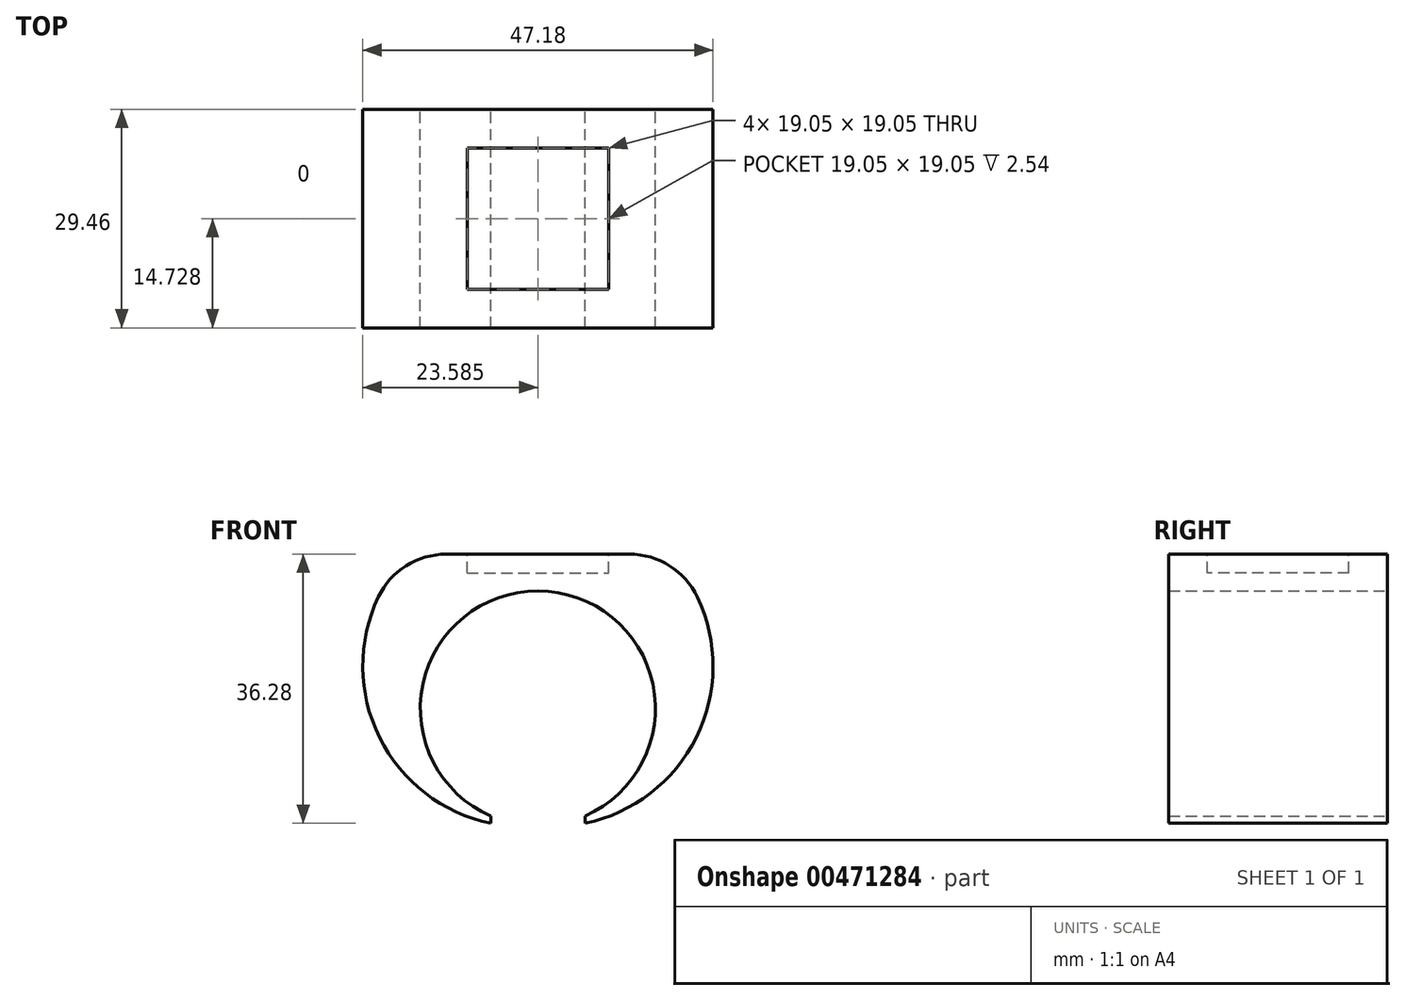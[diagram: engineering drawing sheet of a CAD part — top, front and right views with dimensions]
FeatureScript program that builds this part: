
annotation { "Feature Type Name" : "Feature", "Feature Type Description" : "" }
export const myFeature = defineFeature(function(context is Context, id is Id, definition is map)
    precondition{}
    {
        {
            var Q0;
            Q0=qCreatedBy(makeId("Front.planeOp"),FACE);
            var sketch = newSketch(context, id + "F0", { "sketchPlane" : qUnion([Q0])});
            skLineSegment(sketch, "E0.bottom", {"start": v(-17.46, 2.54) * mm, "end": v(17.46, 2.54) * mm});
            skArc(sketch, "E1", {"start": v(6.35, -32.77) * mm, "mid": v(0, -2.42) * mm, "end": v(-6.35, -32.77) * mm});
            skArc(sketch, "E2", {"start": v(-17.46, 2.54) * mm, "mid": v(-22.64, -18.89) * mm, "end": v(-6.35, -33.74) * mm});
            skArc(sketch, "E3", {"start": v(6.35, -33.74) * mm, "mid": v(22.64, -18.89) * mm, "end": v(17.46, 2.54) * mm});
            skLineSegment(sketch, "E4.trimOffspring", {"start": v(-6.35, -32.77) * mm, "end": v(-6.35, -33.74) * mm});
            skLineSegment(sketch, "E5.trimOffspring", {"start": v(6.35, -32.77) * mm, "end": v(6.35, -33.74) * mm});
            skSolve(sketch);
        }
        {
            var Q0;
            Q0=makeQuery(id+"F0.imprint","IMPRINT",FACE,{"disambiguationData":[TD([[makeQuery(id+"F0.imprint","IMPRINT",EDGE,{"derivedFrom":sQuery(id+"F0.wireOp",EDGE,"E0.bottom")}),-1.0]])]});
            extrude(context, id + "F1", {"entities" : qUnion([Q0]), "depth" : 29.46 * mm});
        }
        {
            var Q0;
            Q0=makeQuery(id+"F1.opExtrude","SWEPT_EDGE",EDGE,{"disambiguationData":[OSD([sQuery(id+"F0.wireOp",EDGE,"E0.bottom"),sQuery(id+"F0.wireOp",EDGE,"E2")])]});
            var Q1;
            Q1=makeQuery(id+"F1.opExtrude","SWEPT_EDGE",EDGE,{"disambiguationData":[OSD([sQuery(id+"F0.wireOp",EDGE,"E0.bottom"),sQuery(id+"F0.wireOp",EDGE,"E3")])]});
            fillet(context, id + "F2", {"entities" : qUnion([Q0, Q1]), "radius" : 10.16 * mm, "tangentPropagation" : true, "allowEdgeOverflow" : false});
        }
        {
            var Q0;
            Q0=makeQuery(id+"F1.opExtrude","SWEPT_FACE",FACE,{"disambiguationData":[OSD([sQuery(id+"F0.wireOp",EDGE,"E0.bottom")])]});
            var sketch = newSketch(context, id + "F3", { "sketchPlane" : qUnion([Q0])});
            skLineSegment(sketch, "E6.bottom", {"start": v(-9.53, -5.2) * mm, "end": v(9.52, -5.2) * mm});
            skLineSegment(sketch, "E6.top", {"start": v(-9.53, -24.26) * mm, "end": v(9.52, -24.26) * mm});
            skLineSegment(sketch, "E6.left", {"start": v(-9.53, -5.2) * mm, "end": v(-9.53, -24.26) * mm});
            skLineSegment(sketch, "E6.right", {"start": v(9.52, -5.2) * mm, "end": v(9.52, -24.26) * mm});
            skSolve(sketch);
        }
        {
            var Q0;
            Q0=makeQuery(id+"F3.imprint","IMPRINT",FACE,{"disambiguationData":[TD([[makeQuery(id+"F3.imprint","IMPRINT",EDGE,{"derivedFrom":sQuery(id+"F3.wireOp",EDGE,"E6.bottom")}),-1.0]])]});
            extrude(context, id + "F4", {"entities" : qUnion([Q0]), "operationType" : NewBodyOperationType.REMOVE, "oppositeDirection" : true, "depth" : 2.54 * mm});
        }
    });
